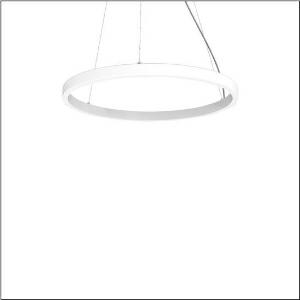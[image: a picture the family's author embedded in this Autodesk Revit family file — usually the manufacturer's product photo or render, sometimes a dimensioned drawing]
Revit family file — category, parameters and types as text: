
# Revit family: silica_r__21_ring-o_5pjbo3d1004a_d373
name_source: partatom
category: Lighting Fixtures
units: mm (PartAtom-declared; Revit-internal decimal feet)

## family parameters
Cut with Voids When Loaded = No
Host = Face
Light Source = No
Part Type = Normal
Room Calculation Point = No
Round Connector Dimension = Use Diameter
Shared = No

## types (1)
- Silica® 21 Ring-O (1 x LED, 6860 lm, 105 W, 3000K)
    Apparent Load = 105 VA
    CIE Flux Codes = 2 16 49 50 100
    Color Rendering = 80
    Color Temperature = 3000K
    Default Elevation = 1800 mm
    Description = Silica® 21 Ring-O, suspended luminaire, of PMMA, frosted, light emission: outer ring side luminous distribution, primary light characteristic: symmetric, installation type: suspended mounting, LED, rated luminous flux: 6.860lm, luminous efficacy: 65lm/W, light colour: 830, colour temperature: 3000K, control gear: DALI 2, with terminal, 5-pole, mains connection: 230V, AC/DC, 0/50..60Hz, rated input power: 105W, housing, of extruded aluminium section, traffic white (RAL 9016), diameter: 1.100mm, ceiling canopy, traffic white (RAL 9016), protection rating (lamp compartment): IP40, insulation class (complete): insulation class I (protective earthing), certification: CE, impact resistance: IK02, permissible operating ambient temperature: 0..+35°C, packaging unit: 1 piece
    Height = 48 mm  [stored 0.15748 ft]
    Lamp = 1 x LED
    Lamp Light Flux = 6860 lm
    Lamp Power = 105 W
    Lamp count = 1
    Length = 1100 mm
    Luminous efficacy = 65 lm/W
    Manufacturer = Siteco
    ModVariant = No
    Model = 5PJBO3D1004A
    Mounting Place = Ceiling
    Mounting Type = Pendant
    Number of Poles = 1
    OnlyDefault = Yes
    Power Factor = 1
    Product Name = Silica® 21 Ring-O
    Product group = suspended luminaire
    ProductGroupID = 905
    Protection Class = Protection class I
    Protection Degree = IP 40
    RLX_Detail_Level = 1
    RLX_Emergency_Light_Flux = 0 lm
    RLX_Emergency_Type = 0
    RLX_Emergency_Type_DB = No
    RlxData = <blob elided: 13549 chars, md5=98c64c76>
    Socket = socket
    Standby Power = 0 W
    System Light Flux = 6860 lm
    System Power = 105 W
    Type Comments = Product without accessories
    Type Image = l_1258387.jpg
    URL = http://relux.com
    VarID = ---
    Voltage = 0 V
    Weight = 0.00 kg
    Width = 0 mm  [stored 0 ft]

note: [stored X ft] marks values corroborated as IEEE doubles in the binary element streams (Revit-internal decimal feet)

## geometry (parser evidence)
native form markers: Sweep x10
no freeform markers — native parametric forms only
